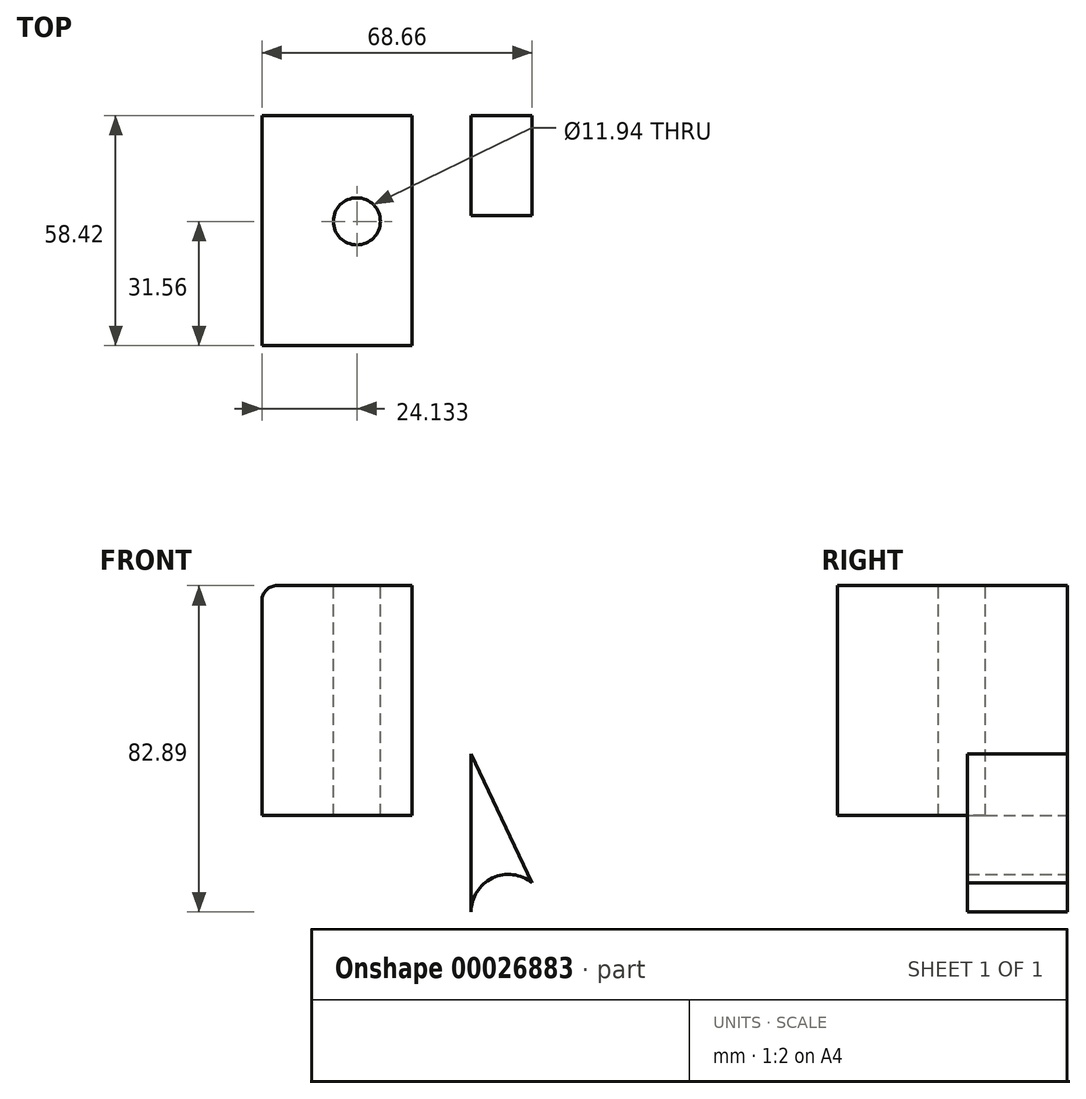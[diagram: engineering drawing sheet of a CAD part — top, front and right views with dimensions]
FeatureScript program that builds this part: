
annotation { "Feature Type Name" : "Feature", "Feature Type Description" : "" }
export const myFeature = defineFeature(function(context is Context, id is Id, definition is map)
    precondition{}
    {
        {
            var Q0;
            Q0=qCreatedBy(makeId("Front.planeOp"),FACE);
            var sketch = newSketch(context, id + "F0", { "sketchPlane" : qUnion([Q0])});
            skCircle(sketch, "E0", {"center": v(0, 0) * mm, "radius": 9.51 * mm});
            skLineSegment(sketch, "E1", {"start": v(-9.51, 0) * mm, "end": v(-9.51, 40.15) * mm});
            skLineSegment(sketch, "E2", {"start": v(-9.51, 40.15) * mm, "end": v(9.51, 0) * mm});
            skLineSegment(sketch, "E3", {"start": v(9.51, 0) * mm, "end": v(9.51, 39.58) * mm});
            skSolve(sketch);
        }
        {
            var Q0;
            {var subQ3=sQuery(id+"F0.wireOp",EDGE,"E1");Q0=makeQuery(id+"F0.imprint","IMPRINT",FACE,{"disambiguationData":[TD([[makeQuery(id+"F0.imprint","IMPRINT",EDGE,{"derivedFrom":subQ3}),-1.0]])]});}
            extrude(context, id + "F1", {"entities" : qUnion([Q0]), "depth" : 25.4 * mm});
        }
        {
            var Q0;
            Q0=qCreatedBy(makeId("Front.planeOp"),FACE);
            var sketch = newSketch(context, id + "F2", { "sketchPlane" : qUnion([Q0])});
            skLineSegment(sketch, "E4.bottom", {"start": v(-58.83, 82.9) * mm, "end": v(-24.54, 82.9) * mm});
            skLineSegment(sketch, "E4.left", {"start": v(-62.64, 79.08) * mm, "end": v(-62.64, 24.47) * mm});
            skLineSegment(sketch, "E4.right", {"start": v(-24.54, 82.9) * mm, "end": v(-24.54, 24.47) * mm});
            skPoint(sketch, "E5.visualSharp", {"position": v(-62.64, 82.9) * mm});
            skArc(sketch, "E5.filletArc", {"start": v(-58.83, 82.9) * mm, "mid": v(-61.52, 81.78) * mm, "end": v(-62.64, 79.08) * mm});
            skLineSegment(sketch, "E6", {"start": v(-62.64, 24.47) * mm, "end": v(-24.54, 24.47) * mm});
            skSolve(sketch);
        }
        {
            var Q0;
            Q0 = qSketchRegion(id + "F2", true);
            extrude(context, id + "F3", {"entities" : qUnion([Q0]), "depth" : 58.42 * mm});
        }
        {
            var Q0;
            Q0=makeQuery(id+"F3.opExtrude","SWEPT_FACE",FACE,{"disambiguationData":[OSD([sQuery(id+"F2.wireOp",EDGE,"E4.bottom")])]});
            var sketch = newSketch(context, id + "F4", { "sketchPlane" : qUnion([Q0])});
            skCircle(sketch, "E7", {"center": v(-38.5, -26.86) * mm, "radius": 5.97 * mm});
            skSolve(sketch);
        }
        {
            var Q0;
            Q0 = qSketchRegion(id + "F4", true);
            extrude(context, id + "F5", {"entities" : qUnion([Q0]), "operationType" : NewBodyOperationType.REMOVE, "oppositeDirection" : true, "depth" : 76.2 * mm});
        }
    });
